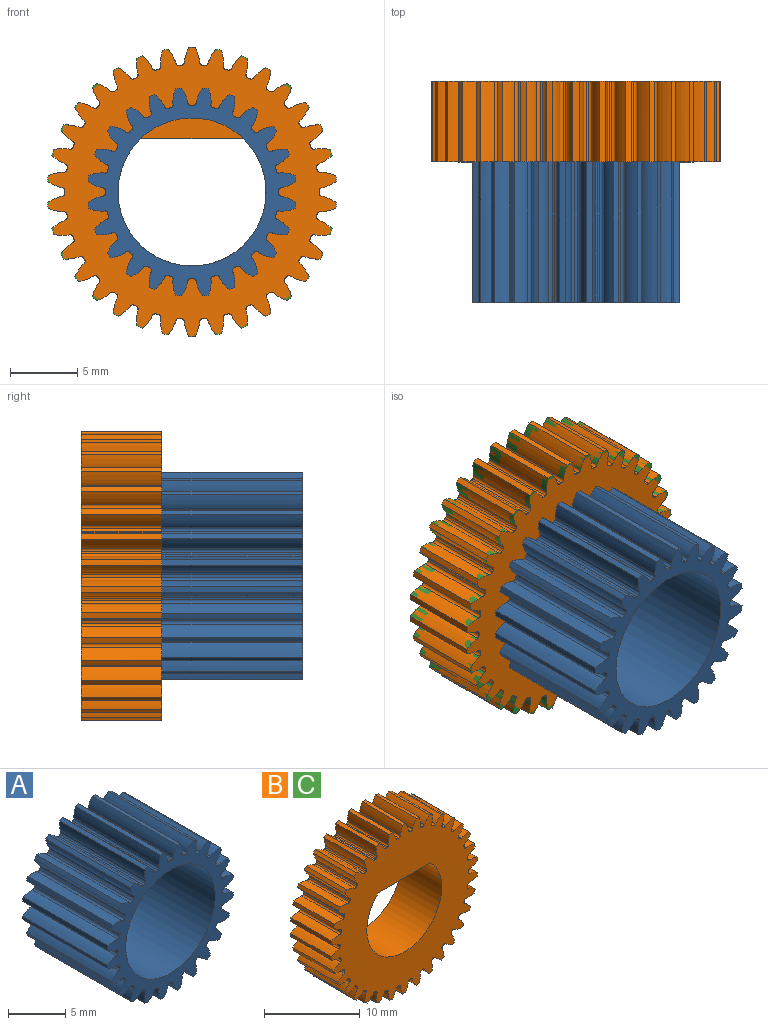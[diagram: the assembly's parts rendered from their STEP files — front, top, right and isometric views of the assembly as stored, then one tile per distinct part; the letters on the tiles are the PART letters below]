
ASSEMBLY  parts=3 mates=1
PART A: 147 faces, bbox 15.5x10.5x15.5 mm
  f0: extruded ~10.5x1.06mm, area 12.3mm2, adj f76,f77,f80,f113
  f1: cylinder r=6.48mm len=10.5mm, axis (0,-1,0), area 2.2mm2, adj f77,f80,f113,f114
  f2: extruded ~10.5x1.06mm, area 12.3mm2, adj f77,f80,f86,f114
  f3: extruded ~10.5x1.15mm, area 12.3mm2, adj f77,f80,f93,f130
  f4: cylinder r=6.48mm len=10.5mm, axis (0,-1,0), area 2.2mm2, adj f77,f80,f129,f130
  f5: extruded ~10.5x0.93mm, area 12.3mm2, adj f77,f80,f94,f129
  f6: extruded ~10.5x1.15mm, area 12.3mm2, adj f77,f80,f92,f128
  f7: cylinder r=6.48mm len=10.5mm, axis (0,-1,0), area 2.2mm2, adj f77,f80,f127,f128
  f8: extruded ~10.5x0.9mm, area 12.3mm2, adj f77,f80,f93,f127
  f9: extruded ~10.5x1.06mm, area 12.3mm2, adj f77,f80,f91,f126
  f10: cylinder r=6.48mm len=10.5mm, axis (0,-1,0), area 2.2mm2, adj f77,f80,f125,f126
  f11: extruded ~10.5x1.06mm, area 12.3mm2, adj f77,f80,f92,f125
  f12: extruded ~10.5x0.9mm, area 12.3mm2, adj f77,f80,f90,f124
  f13: cylinder r=6.48mm len=10.5mm, axis (0,-1,0), area 2.2mm2, adj f77,f80,f123,f124
  f14: extruded ~10.5x1.15mm, area 12.3mm2, adj f77,f80,f91,f123
  f15: extruded ~10.5x1.15mm, area 12.3mm2, adj f77,f80,f87,f118
  f16: cylinder r=6.48mm len=10.5mm, axis (0,-1,0), area 2.2mm2, adj f77,f80,f117,f118
  f17: extruded ~10.5x0.93mm, area 12.3mm2, adj f77,f80,f88,f117
  f18: extruded ~10.5x1.15mm, area 12.3mm2, adj f77,f80,f86,f116
  f19: cylinder r=6.48mm len=10.5mm, axis (0,-1,0), area 2.2mm2, adj f77,f80,f115,f116
  f20: extruded ~10.5x0.9mm, area 12.3mm2, adj f77,f80,f87,f115
  f21: extruded ~10.5x1.08mm, area 12.3mm2, adj f77,f80,f88,f120
  f22: cylinder r=6.48mm len=10.5mm, axis (0,-1,0), area 2.2mm2, adj f77,f80,f119,f120
  f23: extruded ~10.5x1.08mm, area 12.3mm2, adj f77,f80,f89,f119
  f24: extruded ~10.5x0.93mm, area 12.3mm2, adj f77,f80,f89,f122
  f25: cylinder r=6.48mm len=10.5mm, axis (0,-1,0), area 2.2mm2, adj f77,f80,f121,f122
  f26: extruded ~10.5x1.15mm, area 12.3mm2, adj f77,f80,f90,f121
  f27: extruded ~10.5x1.15mm, area 12.3mm2, adj f75,f77,f80,f142
  f28: cylinder r=6.48mm len=10.5mm, axis (0,-1,0), area 2.2mm2, adj f77,f80,f141,f142
  f29: extruded ~10.5x0.93mm, area 12.3mm2, adj f77,f80,f98,f141
  f30: extruded ~10.5x1.15mm, area 12.3mm2, adj f74,f77,f80,f140
  f31: cylinder r=6.48mm len=10.5mm, axis (0,-1,0), area 2.2mm2, adj f77,f80,f139,f140
  f32: extruded ~10.5x0.9mm, area 12.3mm2, adj f75,f77,f80,f139
  f33: extruded ~10.5x1.08mm, area 12.3mm2, adj f77,f80,f98,f144
  f34: cylinder r=6.48mm len=10.5mm, axis (0,-1,0), area 2.2mm2, adj f77,f80,f143,f144
  f35: extruded ~10.5x1.08mm, area 12.3mm2, adj f77,f80,f99,f143
  f36: extruded ~10.5x0.93mm, area 12.3mm2, adj f77,f80,f99,f146
  f37: cylinder r=6.48mm len=10.5mm, axis (0,-1,0), area 2.2mm2, adj f77,f80,f145,f146
  f38: extruded ~10.5x1.15mm, area 12.3mm2, adj f77,f79,f80,f145
  f39: extruded ~10.5x1.06mm, area 12.3mm2, adj f77,f80,f97,f138
  f40: cylinder r=6.48mm len=10.5mm, axis (0,-1,0), area 2.2mm2, adj f77,f80,f137,f138
  f41: extruded ~10.5x1.06mm, area 12.3mm2, adj f74,f77,f80,f137
  f42: extruded ~10.5x0.9mm, area 12.3mm2, adj f77,f80,f96,f136
  f43: cylinder r=6.48mm len=10.5mm, axis (0,-1,0), area 2.2mm2, adj f77,f80,f135,f136
  f44: extruded ~10.5x1.15mm, area 12.3mm2, adj f77,f80,f97,f135
  f45: extruded ~10.5x1.08mm, area 12.3mm2, adj f77,f80,f94,f132
  f46: cylinder r=6.48mm len=10.5mm, axis (0,-1,0), area 2.2mm2, adj f77,f80,f131,f132
  f47: extruded ~10.5x1.08mm, area 12.3mm2, adj f77,f80,f95,f131
  f48: extruded ~10.5x0.93mm, area 12.3mm2, adj f77,f80,f95,f134
  f49: cylinder r=6.48mm len=10.5mm, axis (0,-1,0), area 2.2mm2, adj f77,f80,f133,f134
  f50: extruded ~10.5x1.15mm, area 12.3mm2, adj f77,f80,f96,f133
  f51: extruded ~10.5x1.15mm, area 12.3mm2, adj f77,f80,f101,f108
  f52: cylinder r=6.48mm len=10.5mm, axis (0,-1,0), area 2.2mm2, adj f77,f80,f107,f108
  f53: extruded ~10.5x0.93mm, area 12.3mm2, adj f77,f80,f102,f107
  f54: extruded ~10.5x1.15mm, area 12.3mm2, adj f77,f80,f100,f106
  f55: cylinder r=6.48mm len=10.5mm, axis (0,-1,0), area 2.2mm2, adj f77,f80,f105,f106
  f56: extruded ~10.5x0.9mm, area 12.3mm2, adj f77,f80,f101,f105
  f57: extruded ~10.5x1.06mm, area 12.3mm2, adj f77,f80,f81,f109
  f58: cylinder r=6.48mm len=10.5mm, axis (0,-1,0), area 2.2mm2, adj f77,f80,f109,f110
  f59: extruded ~10.5x1.06mm, area 12.3mm2, adj f77,f80,f100,f110
  f60: extruded ~10.5x0.9mm, area 12.3mm2, adj f77,f79,f80,f111
  f61: cylinder r=6.48mm len=10.5mm, axis (0,-1,0), area 2.2mm2, adj f77,f80,f111,f112
  f62: extruded ~10.5x1.15mm, area 12.3mm2, adj f77,f80,f81,f112
  f63: extruded ~10.5x0.9mm, area 12.3mm2, adj f77,f80,f85,f104
  f64: cylinder r=6.48mm len=10.5mm, axis (0,-1,0), area 2.2mm2, adj f77,f80,f84,f85
  f65: extruded ~10.5x1.15mm, area 12.3mm2, adj f76,f77,f80,f84
  f66: extruded ~10.5x1.08mm, area 12.3mm2, adj f77,f80,f82,f102
  f67: cylinder r=6.48mm len=10.5mm, axis (0,-1,0), area 2.2mm2, adj f77,f80,f82,f83
  f68: extruded ~10.5x1.08mm, area 12.3mm2, adj f77,f80,f83,f103
  f69: extruded ~10.5x0.93mm, area 12.3mm2, adj f72,f77,f80,f103
  f70: cylinder r=6.48mm len=10.5mm, axis (0,-1,0), area 2.2mm2, adj f72,f73,f77,f80
  f71: extruded ~10.5x1.15mm, area 12.3mm2, adj f73,f77,f80,f104
  f72: cylinder r=0.23mm len=10.5mm, axis (0,-1,0), area 3.7mm2, adj f69,f70,f77,f80
  f73: cylinder r=0.23mm len=10.5mm, axis (0,-1,0), area 3.7mm2, adj f70,f71,f77,f80
  f74: cylinder r=7.8mm len=10.5mm, axis (0,-1,0), area 4.5mm2, adj f30,f41,f77,f80
  f75: cylinder r=7.8mm len=10.5mm, axis (0,-1,0), area 4.5mm2, adj f27,f32,f77,f80
  f76: cylinder r=7.8mm len=10.5mm, axis (0,-1,0), area 4.5mm2, adj f0,f65,f77,f80
  f77: plane 15.52x15.52mm, normal (0,1,0), area 64.9mm2, adj f0,f1,f2,f3,f4,f5,f6,f7
  f78: cylinder r=5.53mm len=11.05mm, axis (0,-1,0), area 364.5mm2, adj f77,f80
  f79: cylinder r=7.8mm len=10.5mm, axis (0,-1,0), area 4.5mm2, adj f38,f60,f77,f80
  f80: plane 15.52x15.52mm, normal (0,-1,0), area 64.9mm2, adj f0,f1,f2,f3,f4,f5,f6,f7
  f81: cylinder r=7.8mm len=10.5mm, axis (0,-1,0), area 4.5mm2, adj f57,f62,f77,f80
  f82: cylinder r=0.23mm len=10.5mm, axis (0,-1,0), area 3.7mm2, adj f66,f67,f77,f80
  f83: cylinder r=0.23mm len=10.5mm, axis (0,-1,0), area 3.7mm2, adj f67,f68,f77,f80
  f84: cylinder r=0.23mm len=10.5mm, axis (0,-1,0), area 3.7mm2, adj f64,f65,f77,f80
  f85: cylinder r=0.23mm len=10.5mm, axis (0,-1,0), area 3.7mm2, adj f63,f64,f77,f80
  f86: cylinder r=7.8mm len=10.5mm, axis (0,-1,0), area 4.5mm2, adj f2,f18,f77,f80
  f87: cylinder r=7.8mm len=10.5mm, axis (0,-1,0), area 4.5mm2, adj f15,f20,f77,f80
  f88: cylinder r=7.8mm len=10.5mm, axis (0,-1,0), area 4.5mm2, adj f17,f21,f77,f80
  f89: cylinder r=7.8mm len=10.5mm, axis (0,-1,0), area 4.5mm2, adj f23,f24,f77,f80
  f90: cylinder r=7.8mm len=10.5mm, axis (0,-1,0), area 4.5mm2, adj f12,f26,f77,f80
  f91: cylinder r=7.8mm len=10.5mm, axis (0,-1,0), area 4.5mm2, adj f9,f14,f77,f80
  f92: cylinder r=7.8mm len=10.5mm, axis (0,-1,0), area 4.5mm2, adj f6,f11,f77,f80
  f93: cylinder r=7.8mm len=10.5mm, axis (0,-1,0), area 4.5mm2, adj f3,f8,f77,f80
  f94: cylinder r=7.8mm len=10.5mm, axis (0,-1,0), area 4.5mm2, adj f5,f45,f77,f80
  f95: cylinder r=7.8mm len=10.5mm, axis (0,-1,0), area 4.5mm2, adj f47,f48,f77,f80
  f96: cylinder r=7.8mm len=10.5mm, axis (0,-1,0), area 4.5mm2, adj f42,f50,f77,f80
  f97: cylinder r=7.8mm len=10.5mm, axis (0,-1,0), area 4.5mm2, adj f39,f44,f77,f80
  f98: cylinder r=7.8mm len=10.5mm, axis (0,-1,0), area 4.5mm2, adj f29,f33,f77,f80
  f99: cylinder r=7.8mm len=10.5mm, axis (0,-1,0), area 4.5mm2, adj f35,f36,f77,f80
  f100: cylinder r=7.8mm len=10.5mm, axis (0,-1,0), area 4.5mm2, adj f54,f59,f77,f80
  f101: cylinder r=7.8mm len=10.5mm, axis (0,-1,0), area 4.5mm2, adj f51,f56,f77,f80
  f102: cylinder r=7.8mm len=10.5mm, axis (0,-1,0), area 4.5mm2, adj f53,f66,f77,f80
  f103: cylinder r=7.8mm len=10.5mm, axis (0,-1,0), area 4.5mm2, adj f68,f69,f77,f80
  f104: cylinder r=7.8mm len=10.5mm, axis (0,-1,0), area 4.5mm2, adj f63,f71,f77,f80
  f105: cylinder r=0.23mm len=10.5mm, axis (0,-1,0), area 3.7mm2, adj f55,f56,f77,f80
  f106: cylinder r=0.23mm len=10.5mm, axis (0,-1,0), area 3.7mm2, adj f54,f55,f77,f80
  f107: cylinder r=0.23mm len=10.5mm, axis (0,-1,0), area 3.7mm2, adj f52,f53,f77,f80
  f108: cylinder r=0.23mm len=10.5mm, axis (0,-1,0), area 3.7mm2, adj f51,f52,f77,f80
  f109: cylinder r=0.23mm len=10.5mm, axis (0,-1,0), area 3.7mm2, adj f57,f58,f77,f80
  f110: cylinder r=0.23mm len=10.5mm, axis (0,-1,0), area 3.7mm2, adj f58,f59,f77,f80
  f111: cylinder r=0.23mm len=10.5mm, axis (0,-1,0), area 3.7mm2, adj f60,f61,f77,f80
  f112: cylinder r=0.23mm len=10.5mm, axis (0,-1,0), area 3.7mm2, adj f61,f62,f77,f80
  f113: cylinder r=0.23mm len=10.5mm, axis (0,-1,0), area 3.7mm2, adj f0,f1,f77,f80
  f114: cylinder r=0.23mm len=10.5mm, axis (0,-1,0), area 3.7mm2, adj f1,f2,f77,f80
  f115: cylinder r=0.23mm len=10.5mm, axis (0,-1,0), area 3.7mm2, adj f19,f20,f77,f80
  f116: cylinder r=0.23mm len=10.5mm, axis (0,-1,0), area 3.7mm2, adj f18,f19,f77,f80
  f117: cylinder r=0.23mm len=10.5mm, axis (0,-1,0), area 3.7mm2, adj f16,f17,f77,f80
  f118: cylinder r=0.23mm len=10.5mm, axis (0,-1,0), area 3.7mm2, adj f15,f16,f77,f80
  f119: cylinder r=0.23mm len=10.5mm, axis (0,-1,0), area 3.7mm2, adj f22,f23,f77,f80
  f120: cylinder r=0.23mm len=10.5mm, axis (0,-1,0), area 3.7mm2, adj f21,f22,f77,f80
  f121: cylinder r=0.23mm len=10.5mm, axis (0,-1,0), area 3.7mm2, adj f25,f26,f77,f80
  f122: cylinder r=0.23mm len=10.5mm, axis (0,-1,0), area 3.7mm2, adj f24,f25,f77,f80
  f123: cylinder r=0.23mm len=10.5mm, axis (0,-1,0), area 3.7mm2, adj f13,f14,f77,f80
  f124: cylinder r=0.23mm len=10.5mm, axis (0,-1,0), area 3.7mm2, adj f12,f13,f77,f80
  f125: cylinder r=0.23mm len=10.5mm, axis (0,-1,0), area 3.7mm2, adj f10,f11,f77,f80
  f126: cylinder r=0.23mm len=10.5mm, axis (0,-1,0), area 3.7mm2, adj f9,f10,f77,f80
  f127: cylinder r=0.23mm len=10.5mm, axis (0,-1,0), area 3.7mm2, adj f7,f8,f77,f80
  f128: cylinder r=0.23mm len=10.5mm, axis (0,-1,0), area 3.7mm2, adj f6,f7,f77,f80
  f129: cylinder r=0.23mm len=10.5mm, axis (0,-1,0), area 3.7mm2, adj f4,f5,f77,f80
  f130: cylinder r=0.23mm len=10.5mm, axis (0,-1,0), area 3.7mm2, adj f3,f4,f77,f80
  f131: cylinder r=0.23mm len=10.5mm, axis (0,-1,0), area 3.7mm2, adj f46,f47,f77,f80
  f132: cylinder r=0.23mm len=10.5mm, axis (0,-1,0), area 3.7mm2, adj f45,f46,f77,f80
  f133: cylinder r=0.23mm len=10.5mm, axis (0,-1,0), area 3.7mm2, adj f49,f50,f77,f80
  f134: cylinder r=0.23mm len=10.5mm, axis (0,-1,0), area 3.7mm2, adj f48,f49,f77,f80
  f135: cylinder r=0.23mm len=10.5mm, axis (0,-1,0), area 3.7mm2, adj f43,f44,f77,f80
  f136: cylinder r=0.23mm len=10.5mm, axis (0,-1,0), area 3.7mm2, adj f42,f43,f77,f80
  f137: cylinder r=0.23mm len=10.5mm, axis (0,-1,0), area 3.7mm2, adj f40,f41,f77,f80
  f138: cylinder r=0.23mm len=10.5mm, axis (0,-1,0), area 3.7mm2, adj f39,f40,f77,f80
  f139: cylinder r=0.23mm len=10.5mm, axis (0,-1,0), area 3.7mm2, adj f31,f32,f77,f80
  f140: cylinder r=0.23mm len=10.5mm, axis (0,-1,0), area 3.7mm2, adj f30,f31,f77,f80
  f141: cylinder r=0.23mm len=10.5mm, axis (0,-1,0), area 3.7mm2, adj f28,f29,f77,f80
  f142: cylinder r=0.23mm len=10.5mm, axis (0,-1,0), area 3.7mm2, adj f27,f28,f77,f80
  f143: cylinder r=0.23mm len=10.5mm, axis (0,-1,0), area 3.7mm2, adj f34,f35,f77,f80
  f144: cylinder r=0.23mm len=10.5mm, axis (0,-1,0), area 3.7mm2, adj f33,f34,f77,f80
  f145: cylinder r=0.23mm len=10.5mm, axis (0,-1,0), area 3.7mm2, adj f37,f38,f77,f80
  f146: cylinder r=0.23mm len=10.5mm, axis (0,-1,0), area 3.7mm2, adj f36,f37,f77,f80
PART B: 208 faces, bbox 21.5x6x21.6 mm
  f0: cylinder r=5.53mm len=11.05mm, axis (0,-1,0), area 157.3mm2, adj f103,f108,f207
  f1: extruded ~6x1.11mm, area 7.2mm2, adj f103,f107,f108,f110
  f2: cylinder r=9.48mm len=6mm, axis (0,-1,0), area 1.1mm2, adj f103,f108,f109,f110
  f3: extruded ~6x1.11mm, area 7.2mm2, adj f103,f108,f109,f206
  f4: extruded ~6x1.16mm, area 7.2mm2, adj f103,f108,f116,f182
  f5: cylinder r=9.48mm len=6mm, axis (0,-1,0), area 1.1mm2, adj f103,f108,f115,f116
  f6: extruded ~6x1.04mm, area 7.2mm2, adj f103,f108,f115,f181
  f7: extruded ~6x1.09mm, area 7.2mm2, adj f103,f108,f114,f181
  f8: cylinder r=9.48mm len=6mm, axis (0,-1,0), area 1.1mm2, adj f103,f108,f113,f114
  f9: extruded ~6x1.13mm, area 7.2mm2, adj f103,f108,f113,f178
  f10: extruded ~6x0.86mm, area 7.2mm2, adj f103,f108,f120,f177
  f11: cylinder r=9.48mm len=6mm, axis (0,-1,0), area 1.1mm2, adj f103,f108,f119,f120
  f12: extruded ~6x1.2mm, area 7.2mm2, adj f103,f104,f108,f119
  f13: extruded ~6x0.98mm, area 7.2mm2, adj f103,f108,f118,f178
  f14: cylinder r=9.48mm len=6mm, axis (0,-1,0), area 1.1mm2, adj f103,f108,f117,f118
  f15: extruded ~6x1.18mm, area 7.2mm2, adj f103,f108,f117,f177
  f16: extruded ~6x1.2mm, area 7.2mm2, adj f103,f108,f122,f179
  f17: cylinder r=9.48mm len=6mm, axis (0,-1,0), area 1.1mm2, adj f103,f108,f121,f122
  f18: extruded ~6x0.91mm, area 7.2mm2, adj f103,f108,f121,f182
  f19: extruded ~6x1.19mm, area 7.2mm2, adj f103,f108,f124,f180
  f20: cylinder r=9.48mm len=6mm, axis (0,-1,0), area 1.1mm2, adj f103,f108,f123,f124
  f21: extruded ~6x0.94mm, area 7.2mm2, adj f103,f108,f123,f179
  f22: extruded ~6x1.14mm, area 7.2mm2, adj f103,f108,f126,f183
  f23: cylinder r=9.48mm len=6mm, axis (0,-1,0), area 1.1mm2, adj f103,f108,f125,f126
  f24: extruded ~6x1.06mm, area 7.2mm2, adj f103,f108,f125,f180
  f25: extruded ~6x1.06mm, area 7.2mm2, adj f103,f108,f128,f184
  f26: cylinder r=9.48mm len=6mm, axis (0,-1,0), area 1.1mm2, adj f103,f108,f127,f128
  f27: extruded ~6x1.14mm, area 7.2mm2, adj f103,f108,f127,f183
  f28: extruded ~6x1.18mm, area 7.2mm2, adj f103,f108,f136,f189
  f29: cylinder r=9.48mm len=6mm, axis (0,-1,0), area 1.1mm2, adj f103,f108,f135,f136
  f30: extruded ~6x0.98mm, area 7.2mm2, adj f103,f108,f135,f188
  f31: extruded ~6x1.2mm, area 7.2mm2, adj f103,f108,f134,f190
  f32: cylinder r=9.48mm len=6mm, axis (0,-1,0), area 1.1mm2, adj f103,f108,f133,f134
  f33: extruded ~6x0.86mm, area 7.2mm2, adj f103,f108,f133,f189
  f34: extruded ~6x1.17mm, area 7.2mm2, adj f103,f108,f132,f191
  f35: cylinder r=9.48mm len=6mm, axis (0,-1,0), area 1.1mm2, adj f103,f108,f131,f132
  f36: extruded ~6x1mm, area 7.2mm2, adj f103,f108,f131,f190
  f37: extruded ~6x1.11mm, area 7.2mm2, adj f103,f108,f130,f192
  f38: cylinder r=9.48mm len=6mm, axis (0,-1,0), area 1.1mm2, adj f103,f108,f129,f130
  f39: extruded ~6x1.11mm, area 7.2mm2, adj f103,f108,f129,f191
  f40: extruded ~6x0.94mm, area 7.2mm2, adj f103,f108,f144,f185
  f41: cylinder r=9.48mm len=6mm, axis (0,-1,0), area 1.1mm2, adj f103,f108,f143,f144
  f42: extruded ~6x1.19mm, area 7.2mm2, adj f103,f108,f143,f184
  f43: extruded ~6x0.91mm, area 7.2mm2, adj f103,f108,f142,f186
  f44: cylinder r=9.48mm len=6mm, axis (0,-1,0), area 1.1mm2, adj f103,f108,f141,f142
  f45: extruded ~6x1.2mm, area 7.2mm2, adj f103,f108,f141,f185
  f46: extruded ~6x1.13mm, area 7.2mm2, adj f103,f108,f140,f188
  f47: cylinder r=9.48mm len=6mm, axis (0,-1,0), area 1.1mm2, adj f103,f108,f139,f140
  f48: extruded ~6x1.09mm, area 7.2mm2, adj f103,f108,f139,f187
  f49: extruded ~6x1.04mm, area 7.2mm2, adj f103,f108,f138,f187
  f50: cylinder r=9.48mm len=6mm, axis (0,-1,0), area 1.1mm2, adj f103,f108,f137,f138
  f51: extruded ~6x1.16mm, area 7.2mm2, adj f103,f108,f137,f186
  f52: extruded ~6x1.16mm, area 7.2mm2, adj f103,f108,f152,f197
  f53: cylinder r=9.48mm len=6mm, axis (0,-1,0), area 1.1mm2, adj f103,f108,f151,f152
  f54: extruded ~6x1.04mm, area 7.2mm2, adj f103,f108,f151,f196
  f55: extruded ~6x1.2mm, area 7.2mm2, adj f103,f108,f150,f198
  f56: cylinder r=9.48mm len=6mm, axis (0,-1,0), area 1.1mm2, adj f103,f108,f149,f150
  f57: extruded ~6x0.91mm, area 7.2mm2, adj f103,f108,f149,f197
  f58: extruded ~6x1.19mm, area 7.2mm2, adj f103,f108,f148,f199
  f59: cylinder r=9.48mm len=6mm, axis (0,-1,0), area 1.1mm2, adj f103,f108,f147,f148
  f60: extruded ~6x0.94mm, area 7.2mm2, adj f103,f108,f147,f198
  f61: extruded ~6x1.14mm, area 7.2mm2, adj f103,f108,f146,f200
  f62: cylinder r=9.48mm len=6mm, axis (0,-1,0), area 1.1mm2, adj f103,f108,f145,f146
  f63: extruded ~6x1.06mm, area 7.2mm2, adj f103,f108,f145,f199
  f64: extruded ~6x1mm, area 7.2mm2, adj f103,f108,f160,f193
  f65: cylinder r=9.48mm len=6mm, axis (0,-1,0), area 1.1mm2, adj f103,f108,f159,f160
  f66: extruded ~6x1.17mm, area 7.2mm2, adj f103,f108,f159,f192
  f67: extruded ~6x0.86mm, area 7.2mm2, adj f103,f108,f158,f194
  f68: cylinder r=9.48mm len=6mm, axis (0,-1,0), area 1.1mm2, adj f103,f108,f157,f158
  f69: extruded ~6x1.2mm, area 7.2mm2, adj f103,f108,f157,f193
  f70: extruded ~6x1.09mm, area 7.2mm2, adj f103,f108,f156,f196
  f71: cylinder r=9.48mm len=6mm, axis (0,-1,0), area 1.1mm2, adj f103,f108,f155,f156
  f72: extruded ~6x1.13mm, area 7.2mm2, adj f103,f108,f155,f195
  f73: extruded ~6x0.98mm, area 7.2mm2, adj f103,f108,f154,f195
  f74: cylinder r=9.48mm len=6mm, axis (0,-1,0), area 1.1mm2, adj f103,f108,f153,f154
  f75: extruded ~6x1.18mm, area 7.2mm2, adj f103,f108,f153,f194
  f76: extruded ~6x1.18mm, area 7.2mm2, adj f103,f108,f168,f204
  f77: cylinder r=9.48mm len=6mm, axis (0,-1,0), area 1.1mm2, adj f103,f108,f167,f168
  f78: extruded ~6x0.98mm, area 7.2mm2, adj f103,f108,f167,f203
  f79: extruded ~6x1.13mm, area 7.2mm2, adj f103,f108,f166,f203
  f80: cylinder r=9.48mm len=6mm, axis (0,-1,0), area 1.1mm2, adj f103,f108,f165,f166
  f81: extruded ~6x1.09mm, area 7.2mm2, adj f103,f108,f165,f202
  f82: extruded ~6x1.2mm, area 7.2mm2, adj f103,f108,f164,f205
  f83: cylinder r=9.48mm len=6mm, axis (0,-1,0), area 1.1mm2, adj f103,f108,f163,f164
  f84: extruded ~6x0.86mm, area 7.2mm2, adj f103,f108,f163,f204
  f85: extruded ~6x1.17mm, area 7.2mm2, adj f103,f108,f162,f206
  f86: cylinder r=9.48mm len=6mm, axis (0,-1,0), area 1.1mm2, adj f103,f108,f161,f162
  f87: extruded ~6x1mm, area 7.2mm2, adj f103,f108,f161,f205
  f88: extruded ~6x1.06mm, area 7.2mm2, adj f103,f105,f108,f176
  f89: cylinder r=9.48mm len=6mm, axis (0,-1,0), area 1.1mm2, adj f103,f108,f175,f176
  f90: extruded ~6x1.14mm, area 7.2mm2, adj f103,f108,f175,f200
  f91: extruded ~6x0.94mm, area 7.2mm2, adj f103,f106,f108,f174
  f92: cylinder r=9.48mm len=6mm, axis (0,-1,0), area 1.1mm2, adj f103,f108,f173,f174
  f93: extruded ~6x1.19mm, area 7.2mm2, adj f103,f105,f108,f173
  f94: extruded ~6x0.91mm, area 7.2mm2, adj f103,f108,f172,f201
  f95: cylinder r=9.48mm len=6mm, axis (0,-1,0), area 1.1mm2, adj f103,f108,f171,f172
  f96: extruded ~6x1.2mm, area 7.2mm2, adj f103,f106,f108,f171
  f97: extruded ~6x1.04mm, area 7.2mm2, adj f103,f108,f170,f202
  f98: cylinder r=9.48mm len=6mm, axis (0,-1,0), area 1.1mm2, adj f103,f108,f169,f170
  f99: extruded ~6x1.16mm, area 7.2mm2, adj f103,f108,f169,f201
  f100: extruded ~6x1mm, area 7.2mm2, adj f103,f104,f108,f112
  f101: cylinder r=9.48mm len=6mm, axis (0,-1,0), area 1.1mm2, adj f103,f108,f111,f112
  f102: extruded ~6x1.17mm, area 7.2mm2, adj f103,f107,f108,f111
  f103: plane 21.6x21.54mm, normal (0,-1,0), area 236.7mm2, adj f0,f1,f2,f3,f4,f5,f6,f7
  f104: cylinder r=10.8mm len=6mm, axis (0,-1,0), area 2.7mm2, adj f12,f100,f103,f108
  f105: cylinder r=10.8mm len=6mm, axis (0,-1,0), area 2.7mm2, adj f88,f93,f103,f108
  f106: cylinder r=10.8mm len=6mm, axis (0,-1,0), area 2.7mm2, adj f91,f96,f103,f108
  f107: cylinder r=10.8mm len=6mm, axis (0,-1,0), area 2.7mm2, adj f1,f102,f103,f108
  f108: plane 21.6x21.54mm, normal (0,1,0), area 236.7mm2, adj f0,f1,f2,f3,f4,f5,f6,f7
  f109: cylinder r=0.22mm len=6mm, axis (0,-1,0), area 1.9mm2, adj f2,f3,f103,f108
  f110: cylinder r=0.22mm len=6mm, axis (0,-1,0), area 1.9mm2, adj f1,f2,f103,f108
  f111: cylinder r=0.22mm len=6mm, axis (0,-1,0), area 1.9mm2, adj f101,f102,f103,f108
  f112: cylinder r=0.22mm len=6mm, axis (0,-1,0), area 1.9mm2, adj f100,f101,f103,f108
  f113: cylinder r=0.22mm len=6mm, axis (0,-1,0), area 1.9mm2, adj f8,f9,f103,f108
  f114: cylinder r=0.22mm len=6mm, axis (0,-1,0), area 1.9mm2, adj f7,f8,f103,f108
  f115: cylinder r=0.22mm len=6mm, axis (0,-1,0), area 1.9mm2, adj f5,f6,f103,f108
  f116: cylinder r=0.22mm len=6mm, axis (0,-1,0), area 1.9mm2, adj f4,f5,f103,f108
  f117: cylinder r=0.22mm len=6mm, axis (0,-1,0), area 1.9mm2, adj f14,f15,f103,f108
  f118: cylinder r=0.22mm len=6mm, axis (0,-1,0), area 1.9mm2, adj f13,f14,f103,f108
  f119: cylinder r=0.22mm len=6mm, axis (0,-1,0), area 1.9mm2, adj f11,f12,f103,f108
  f120: cylinder r=0.22mm len=6mm, axis (0,-1,0), area 1.9mm2, adj f10,f11,f103,f108
  f121: cylinder r=0.22mm len=6mm, axis (0,-1,0), area 1.9mm2, adj f17,f18,f103,f108
  f122: cylinder r=0.22mm len=6mm, axis (0,-1,0), area 1.9mm2, adj f16,f17,f103,f108
  f123: cylinder r=0.22mm len=6mm, axis (0,-1,0), area 1.9mm2, adj f20,f21,f103,f108
  f124: cylinder r=0.22mm len=6mm, axis (0,-1,0), area 1.9mm2, adj f19,f20,f103,f108
  f125: cylinder r=0.22mm len=6mm, axis (0,-1,0), area 1.9mm2, adj f23,f24,f103,f108
  f126: cylinder r=0.22mm len=6mm, axis (0,-1,0), area 1.9mm2, adj f22,f23,f103,f108
  f127: cylinder r=0.22mm len=6mm, axis (0,-1,0), area 1.9mm2, adj f26,f27,f103,f108
  f128: cylinder r=0.22mm len=6mm, axis (0,-1,0), area 1.9mm2, adj f25,f26,f103,f108
  f129: cylinder r=0.22mm len=6mm, axis (0,-1,0), area 1.9mm2, adj f38,f39,f103,f108
  f130: cylinder r=0.22mm len=6mm, axis (0,-1,0), area 1.9mm2, adj f37,f38,f103,f108
  f131: cylinder r=0.22mm len=6mm, axis (0,-1,0), area 1.9mm2, adj f35,f36,f103,f108
  f132: cylinder r=0.22mm len=6mm, axis (0,-1,0), area 1.9mm2, adj f34,f35,f103,f108
  f133: cylinder r=0.22mm len=6mm, axis (0,-1,0), area 1.9mm2, adj f32,f33,f103,f108
  f134: cylinder r=0.22mm len=6mm, axis (0,-1,0), area 1.9mm2, adj f31,f32,f103,f108
  f135: cylinder r=0.22mm len=6mm, axis (0,-1,0), area 1.9mm2, adj f29,f30,f103,f108
  f136: cylinder r=0.22mm len=6mm, axis (0,-1,0), area 1.9mm2, adj f28,f29,f103,f108
  f137: cylinder r=0.22mm len=6mm, axis (0,-1,0), area 1.9mm2, adj f50,f51,f103,f108
  f138: cylinder r=0.22mm len=6mm, axis (0,-1,0), area 1.9mm2, adj f49,f50,f103,f108
  f139: cylinder r=0.22mm len=6mm, axis (0,-1,0), area 1.9mm2, adj f47,f48,f103,f108
  f140: cylinder r=0.22mm len=6mm, axis (0,-1,0), area 1.9mm2, adj f46,f47,f103,f108
  f141: cylinder r=0.22mm len=6mm, axis (0,-1,0), area 1.9mm2, adj f44,f45,f103,f108
  f142: cylinder r=0.22mm len=6mm, axis (0,-1,0), area 1.9mm2, adj f43,f44,f103,f108
  f143: cylinder r=0.22mm len=6mm, axis (0,-1,0), area 1.9mm2, adj f41,f42,f103,f108
  f144: cylinder r=0.22mm len=6mm, axis (0,-1,0), area 1.9mm2, adj f40,f41,f103,f108
  f145: cylinder r=0.22mm len=6mm, axis (0,-1,0), area 1.9mm2, adj f62,f63,f103,f108
  f146: cylinder r=0.22mm len=6mm, axis (0,-1,0), area 1.9mm2, adj f61,f62,f103,f108
  f147: cylinder r=0.22mm len=6mm, axis (0,-1,0), area 1.9mm2, adj f59,f60,f103,f108
  f148: cylinder r=0.22mm len=6mm, axis (0,-1,0), area 1.9mm2, adj f58,f59,f103,f108
  f149: cylinder r=0.22mm len=6mm, axis (0,-1,0), area 1.9mm2, adj f56,f57,f103,f108
  f150: cylinder r=0.22mm len=6mm, axis (0,-1,0), area 1.9mm2, adj f55,f56,f103,f108
  f151: cylinder r=0.22mm len=6mm, axis (0,-1,0), area 1.9mm2, adj f53,f54,f103,f108
  f152: cylinder r=0.22mm len=6mm, axis (0,-1,0), area 1.9mm2, adj f52,f53,f103,f108
  f153: cylinder r=0.22mm len=6mm, axis (0,-1,0), area 1.9mm2, adj f74,f75,f103,f108
  f154: cylinder r=0.22mm len=6mm, axis (0,-1,0), area 1.9mm2, adj f73,f74,f103,f108
  f155: cylinder r=0.22mm len=6mm, axis (0,-1,0), area 1.9mm2, adj f71,f72,f103,f108
  f156: cylinder r=0.22mm len=6mm, axis (0,-1,0), area 1.9mm2, adj f70,f71,f103,f108
  f157: cylinder r=0.22mm len=6mm, axis (0,-1,0), area 1.9mm2, adj f68,f69,f103,f108
  f158: cylinder r=0.22mm len=6mm, axis (0,-1,0), area 1.9mm2, adj f67,f68,f103,f108
  f159: cylinder r=0.22mm len=6mm, axis (0,-1,0), area 1.9mm2, adj f65,f66,f103,f108
  f160: cylinder r=0.22mm len=6mm, axis (0,-1,0), area 1.9mm2, adj f64,f65,f103,f108
  f161: cylinder r=0.22mm len=6mm, axis (0,-1,0), area 1.9mm2, adj f86,f87,f103,f108
  f162: cylinder r=0.22mm len=6mm, axis (0,-1,0), area 1.9mm2, adj f85,f86,f103,f108
  f163: cylinder r=0.22mm len=6mm, axis (0,-1,0), area 1.9mm2, adj f83,f84,f103,f108
  f164: cylinder r=0.22mm len=6mm, axis (0,-1,0), area 1.9mm2, adj f82,f83,f103,f108
  f165: cylinder r=0.22mm len=6mm, axis (0,-1,0), area 1.9mm2, adj f80,f81,f103,f108
  f166: cylinder r=0.22mm len=6mm, axis (0,-1,0), area 1.9mm2, adj f79,f80,f103,f108
  f167: cylinder r=0.22mm len=6mm, axis (0,-1,0), area 1.9mm2, adj f77,f78,f103,f108
  f168: cylinder r=0.22mm len=6mm, axis (0,-1,0), area 1.9mm2, adj f76,f77,f103,f108
  f169: cylinder r=0.22mm len=6mm, axis (0,-1,0), area 1.9mm2, adj f98,f99,f103,f108
  f170: cylinder r=0.22mm len=6mm, axis (0,-1,0), area 1.9mm2, adj f97,f98,f103,f108
  f171: cylinder r=0.22mm len=6mm, axis (0,-1,0), area 1.9mm2, adj f95,f96,f103,f108
  f172: cylinder r=0.22mm len=6mm, axis (0,-1,0), area 1.9mm2, adj f94,f95,f103,f108
  f173: cylinder r=0.22mm len=6mm, axis (0,-1,0), area 1.9mm2, adj f92,f93,f103,f108
  f174: cylinder r=0.22mm len=6mm, axis (0,-1,0), area 1.9mm2, adj f91,f92,f103,f108
  f175: cylinder r=0.22mm len=6mm, axis (0,-1,0), area 1.9mm2, adj f89,f90,f103,f108
  f176: cylinder r=0.22mm len=6mm, axis (0,-1,0), area 1.9mm2, adj f88,f89,f103,f108
  f177: cylinder r=10.8mm len=6mm, axis (0,-1,0), area 2.7mm2, adj f10,f15,f103,f108
  f178: cylinder r=10.8mm len=6mm, axis (0,-1,0), area 2.7mm2, adj f9,f13,f103,f108
  f179: cylinder r=10.8mm len=6mm, axis (0,-1,0), area 2.7mm2, adj f16,f21,f103,f108
  f180: cylinder r=10.8mm len=6mm, axis (0,-1,0), area 2.7mm2, adj f19,f24,f103,f108
  f181: cylinder r=10.8mm len=6mm, axis (0,-1,0), area 2.7mm2, adj f6,f7,f103,f108
  f182: cylinder r=10.8mm len=6mm, axis (0,-1,0), area 2.7mm2, adj f4,f18,f103,f108
  f183: cylinder r=10.8mm len=6mm, axis (0,-1,0), area 2.7mm2, adj f22,f27,f103,f108
  f184: cylinder r=10.8mm len=6mm, axis (0,-1,0), area 2.7mm2, adj f25,f42,f103,f108
  f185: cylinder r=10.8mm len=6mm, axis (0,-1,0), area 2.7mm2, adj f40,f45,f103,f108
  f186: cylinder r=10.8mm len=6mm, axis (0,-1,0), area 2.7mm2, adj f43,f51,f103,f108
  f187: cylinder r=10.8mm len=6mm, axis (0,-1,0), area 2.7mm2, adj f48,f49,f103,f108
  f188: cylinder r=10.8mm len=6mm, axis (0,-1,0), area 2.7mm2, adj f30,f46,f103,f108
  f189: cylinder r=10.8mm len=6mm, axis (0,-1,0), area 2.7mm2, adj f28,f33,f103,f108
  f190: cylinder r=10.8mm len=6mm, axis (0,-1,0), area 2.7mm2, adj f31,f36,f103,f108
  f191: cylinder r=10.8mm len=6mm, axis (0,-1,0), area 2.7mm2, adj f34,f39,f103,f108
  f192: cylinder r=10.8mm len=6mm, axis (0,-1,0), area 2.7mm2, adj f37,f66,f103,f108
  f193: cylinder r=10.8mm len=6mm, axis (0,-1,0), area 2.7mm2, adj f64,f69,f103,f108
  f194: cylinder r=10.8mm len=6mm, axis (0,-1,0), area 2.7mm2, adj f67,f75,f103,f108
  f195: cylinder r=10.8mm len=6mm, axis (0,-1,0), area 2.7mm2, adj f72,f73,f103,f108
  f196: cylinder r=10.8mm len=6mm, axis (0,-1,0), area 2.7mm2, adj f54,f70,f103,f108
  f197: cylinder r=10.8mm len=6mm, axis (0,-1,0), area 2.7mm2, adj f52,f57,f103,f108
  f198: cylinder r=10.8mm len=6mm, axis (0,-1,0), area 2.7mm2, adj f55,f60,f103,f108
  f199: cylinder r=10.8mm len=6mm, axis (0,-1,0), area 2.7mm2, adj f58,f63,f103,f108
  f200: cylinder r=10.8mm len=6mm, axis (0,-1,0), area 2.7mm2, adj f61,f90,f103,f108
  f201: cylinder r=10.8mm len=6mm, axis (0,-1,0), area 2.7mm2, adj f94,f99,f103,f108
  f202: cylinder r=10.8mm len=6mm, axis (0,-1,0), area 2.7mm2, adj f81,f97,f103,f108
  f203: cylinder r=10.8mm len=6mm, axis (0,-1,0), area 2.7mm2, adj f78,f79,f103,f108
  f204: cylinder r=10.8mm len=6mm, axis (0,-1,0), area 2.7mm2, adj f76,f84,f103,f108
  f205: cylinder r=10.8mm len=6mm, axis (0,-1,0), area 2.7mm2, adj f82,f87,f103,f108
  f206: cylinder r=10.8mm len=6mm, axis (0,-1,0), area 2.7mm2, adj f3,f85,f103,f108
  f207: plane 7.68x6mm, normal (0,0,-1), area 46.1mm2, adj f0,f103,f108
PART C: same geometry as B
PLACE A t=(-7.19,6.71,-1.71)mm
PLACE B t=(-7.19,12.71,-1.71)mm
PLACE C t=(-7.19,12.71,-1.71)mm
MATE planar A.f1 <-> B.f0  axis (0,1,0) through (-7.19,-8.29,-1.71)mm
